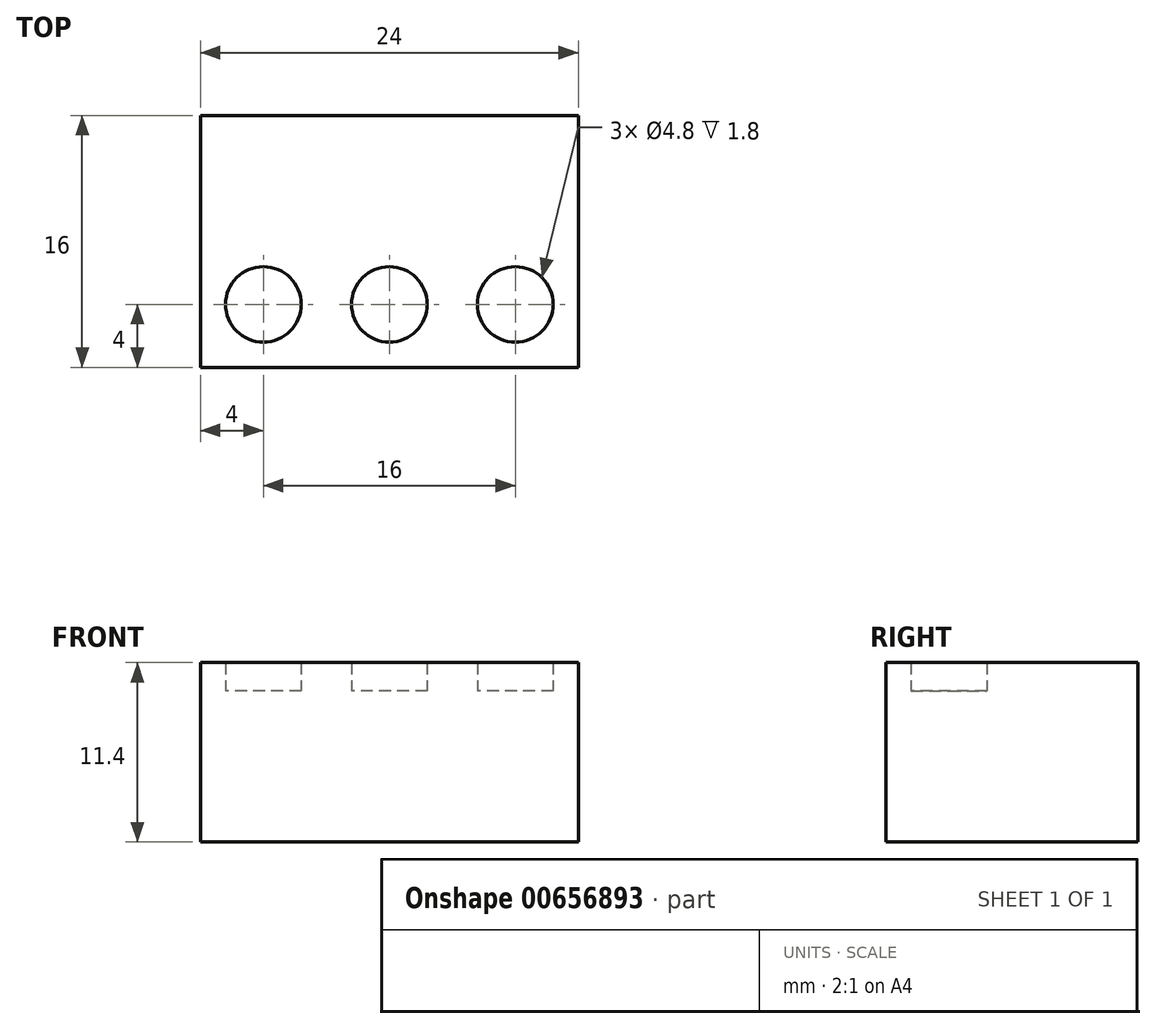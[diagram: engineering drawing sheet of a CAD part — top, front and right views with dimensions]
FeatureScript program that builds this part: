
annotation { "Feature Type Name" : "Feature", "Feature Type Description" : "" }
export const myFeature = defineFeature(function(context is Context, id is Id, definition is map)
    precondition{}
    {
        {
            var Q0;
            Q0=qCreatedBy(makeId("Top.planeOp"),FACE);
            var sketch = newSketch(context, id + "F0", { "sketchPlane" : qUnion([Q0])});
            skLineSegment(sketch, "E0.bottom", {"start": v(0, 0) * mm, "end": v(-24, 0) * mm});
            skLineSegment(sketch, "E0.top", {"start": v(0, 16) * mm, "end": v(-24, 16) * mm});
            skLineSegment(sketch, "E0.left", {"start": v(0, 0) * mm, "end": v(0, 16) * mm});
            skLineSegment(sketch, "E0.right", {"start": v(-24, 0) * mm, "end": v(-24, 16) * mm});
            skSolve(sketch);
        }
        {
            var Q0;
            Q0=makeQuery(id+"F0.imprint","IMPRINT",FACE,{"disambiguationData":[TD([[makeQuery(id+"F0.imprint","IMPRINT",EDGE,{"derivedFrom":sQuery(id+"F0.wireOp",EDGE,"E0.bottom")}),-1.0]])]});
            extrude(context, id + "F1", {"entities" : qUnion([Q0]), "depth" : 9.6 * mm, "offsetDistance" : 25.4 * mm});
        }
        {
            var Q0;
            Q0=makeQuery(id+"F1.opExtrude","CAP_FACE",FACE,{"disambiguationData":[OSD([sQuery(id+"F0.wireOp",EDGE,"E0.bottom"),sQuery(id+"F0.wireOp",EDGE,"E0.top"),sQuery(id+"F0.wireOp",EDGE,"E0.left"),sQuery(id+"F0.wireOp",EDGE,"E0.right")])],"isStart":false});
            var sketch = newSketch(context, id + "F2", { "sketchPlane" : qUnion([Q0])});
            skLineSegment(sketch, "E1", {"start": v(-24, 8) * mm, "end": v(0, 8) * mm, "construction": true});
            skLineSegment(sketch, "E2", {"start": v(-16, 16) * mm, "end": v(-16, 0) * mm, "construction": true});
            skLineSegment(sketch, "E3", {"start": v(-8, 16) * mm, "end": v(-8, 0) * mm, "construction": true});
            skLineSegment(sketch, "E4", {"start": v(-24, 16) * mm, "end": v(-16, 8) * mm, "construction": true});
            skLineSegment(sketch, "E5", {"start": v(-16, 8) * mm, "end": v(-8, 16) * mm, "construction": true});
            skLineSegment(sketch, "E6", {"start": v(-8, 16) * mm, "end": v(0, 8) * mm, "construction": true});
            skCircle(sketch, "E7", {"center": v(-20, 12) * mm, "radius": 2.4 * mm});
            skCircle(sketch, "E8", {"center": v(-12, 12) * mm, "radius": 2.4 * mm});
            skCircle(sketch, "E9", {"center": v(-4, 12) * mm, "radius": 2.4 * mm});
            skCircle(sketch, "E10.MirrorC", {"center": v(-20, 4) * mm, "radius": 2.4 * mm});
            skCircle(sketch, "E11.MirrorC", {"center": v(-12, 4) * mm, "radius": 2.4 * mm});
            skCircle(sketch, "E12.MirrorC", {"center": v(-4, 4) * mm, "radius": 2.4 * mm});
            skSolve(sketch);
        }
        {
            var Q0;
            Q0=makeQuery(id+"F2.imprint","IMPRINT",FACE,{"disambiguationData":[TD([[makeQuery(id+"F2.imprint","IMPRINT",EDGE,{"derivedFrom":sQuery(id+"F2.wireOp",EDGE,"E9")}),1.0]])]});
            var Q1;
            Q1=makeQuery(id+"F2.imprint","IMPRINT",FACE,{"disambiguationData":[TD([[makeQuery(id+"F2.imprint","IMPRINT",EDGE,{"derivedFrom":sQuery(id+"F2.wireOp",EDGE,"E12.MirrorC")}),-1.0]])]});
            var Q2;
            Q2=makeQuery(id+"F2.imprint","IMPRINT",FACE,{"disambiguationData":[TD([[makeQuery(id+"F2.imprint","IMPRINT",EDGE,{"derivedFrom":sQuery(id+"F2.wireOp",EDGE,"E11.MirrorC")}),-1.0]])]});
            var Q3;
            Q3=makeQuery(id+"F2.imprint","IMPRINT",FACE,{"disambiguationData":[TD([[makeQuery(id+"F2.imprint","IMPRINT",EDGE,{"derivedFrom":sQuery(id+"F2.wireOp",EDGE,"E10.MirrorC")}),-1.0]])]});
            var Q4;
            Q4=makeQuery(id+"F2.imprint","IMPRINT",FACE,{"disambiguationData":[TD([[makeQuery(id+"F2.imprint","IMPRINT",EDGE,{"derivedFrom":sQuery(id+"F2.wireOp",EDGE,"E7")}),1.0]])]});
            var Q5;
            Q5=makeQuery(id+"F2.imprint","IMPRINT",FACE,{"disambiguationData":[TD([[makeQuery(id+"F2.imprint","IMPRINT",EDGE,{"derivedFrom":sQuery(id+"F2.wireOp",EDGE,"E8")}),1.0]])]});
            extrude(context, id + "F3", {"entities" : qUnion([Q0, Q1, Q2, Q3, Q4, Q5]), "operationType" : NewBodyOperationType.ADD, "depth" : 1.8 * mm, "offsetDistance" : 25.4 * mm});
        }
    });
